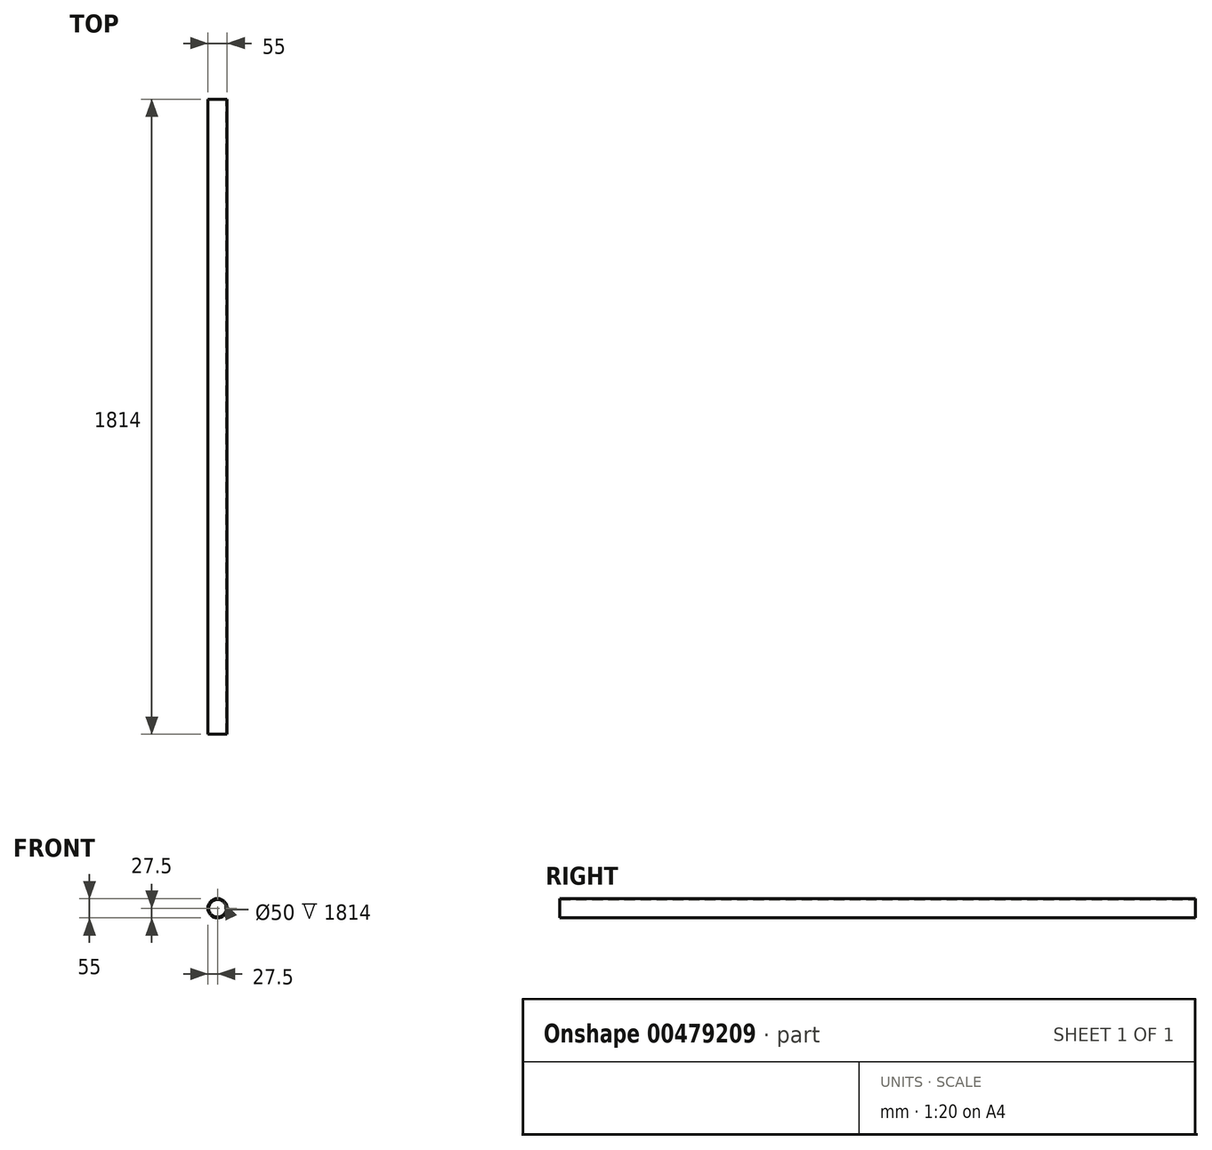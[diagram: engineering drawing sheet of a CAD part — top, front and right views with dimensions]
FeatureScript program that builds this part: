
annotation { "Feature Type Name" : "Feature", "Feature Type Description" : "" }
export const myFeature = defineFeature(function(context is Context, id is Id, definition is map)
    precondition{}
    {
        {
            var Q0;
            Q0=qCreatedBy(makeId("Front.planeOp"),FACE);
            var sketch = newSketch(context, id + "F0", { "sketchPlane" : qUnion([Q0])});
            skCircle(sketch, "E0", {"center": v(0, 0) * mm, "radius": 25 * mm});
            skCircle(sketch, "E1", {"center": v(0, 0) * mm, "radius": 27.5 * mm});
            skSolve(sketch);
        }
        {
            var Q0;
            Q0=makeQuery(id+"F0.imprint","IMPRINT",FACE,{"disambiguationData":[TD([[makeQuery(id+"F0.imprint","IMPRINT",EDGE,{"derivedFrom":sQuery(id+"F0.wireOp",EDGE,"E0")}),-1.0]])]});
            extrude(context, id + "F1", {"entities" : qUnion([Q0]), "depth" : 1814 * mm, "offsetDistance" : 25 * mm});
        }
    });
